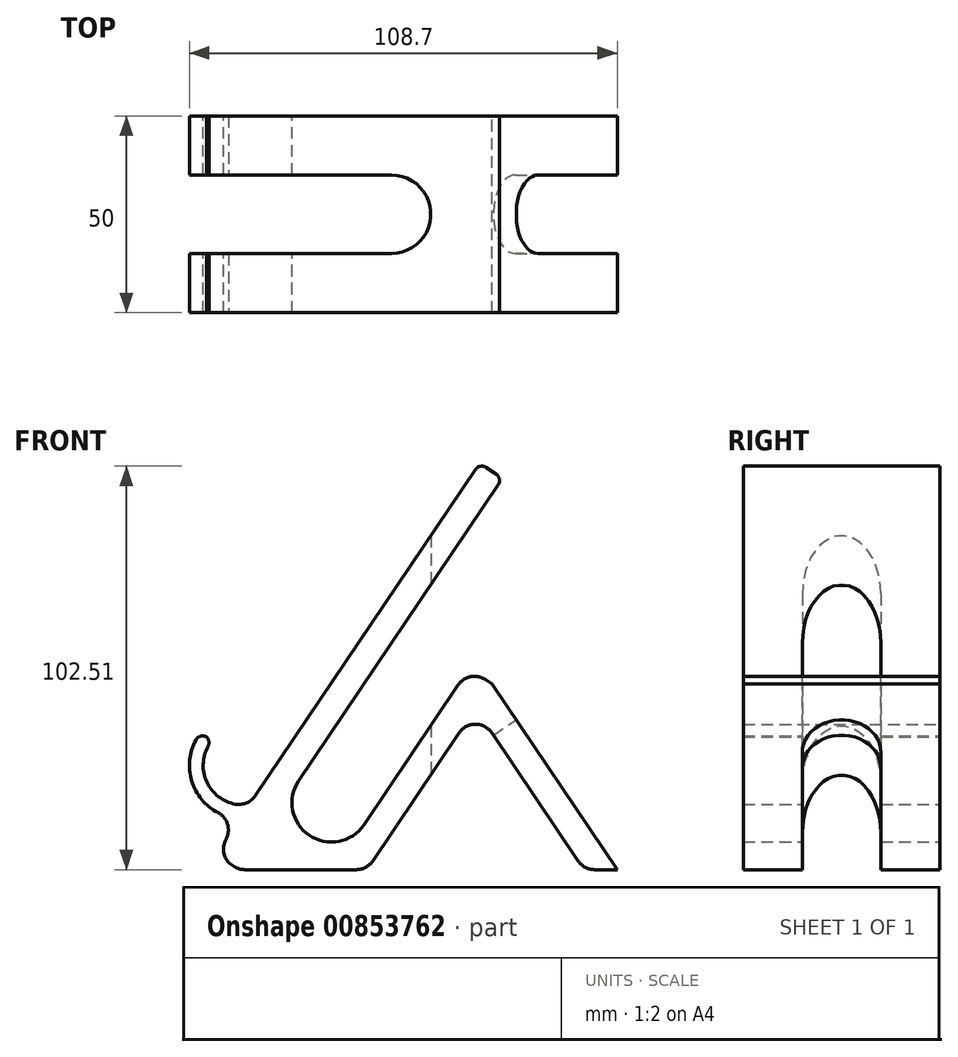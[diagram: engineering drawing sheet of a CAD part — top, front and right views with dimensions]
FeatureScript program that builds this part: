
annotation { "Feature Type Name" : "Feature", "Feature Type Description" : "" }
export const myFeature = defineFeature(function(context is Context, id is Id, definition is map)
    precondition{}
    {
        {
            var Q0;
            Q0=qCreatedBy(makeId("Front.planeOp"),FACE);
            var sketch = newSketch(context, id + "F0", { "sketchPlane" : qUnion([Q0])});
            skLineSegment(sketch, "E0", {"start": v(15.24, 22.6) * mm, "end": v(67.03, 99.37) * mm});
            skLineSegment(sketch, "E1", {"start": v(67.03, 99.37) * mm, "end": v(61.22, 103.29) * mm});
            skLineSegment(sketch, "E2", {"start": v(61.22, 103.29) * mm, "end": v(2.78, 16.63) * mm});
            skLineSegment(sketch, "E3", {"start": v(-5.88, 3.8) * mm, "end": v(0, 0) * mm});
            skArc(sketch, "E4", {"start": v(15.24, 22.6) * mm, "mid": v(17.94, 8.7) * mm, "end": v(31.82, 11.4) * mm});
            skLineSegment(sketch, "E5", {"start": v(-35.19, 0) * mm, "end": v(113.44, 0) * mm, "construction": true});
            skLineSegment(sketch, "E6", {"start": v(31.82, 11.4) * mm, "end": v(58.57, 51.06) * mm});
            skLineSegment(sketch, "E7", {"start": v(58.57, 51.06) * mm, "end": v(64.37, 47.15) * mm});
            skLineSegment(sketch, "E8", {"start": v(60.15, 40.89) * mm, "end": v(32.57, 0) * mm});
            skLineSegment(sketch, "E9", {"start": v(32.57, 0) * mm, "end": v(0, 0) * mm});
            skLineSegment(sketch, "E10", {"start": v(64.37, 47.15) * mm, "end": v(96.17, 0) * mm});
            skLineSegment(sketch, "E11", {"start": v(60.15, 40.89) * mm, "end": v(87.73, 0) * mm});
            skLineSegment(sketch, "E12", {"start": v(87.73, 0) * mm, "end": v(96.17, 0) * mm});
            skLineSegment(sketch, "E13", {"start": v(53.8, 104.81) * mm, "end": v(-7.27, 14.27) * mm, "construction": true});
            skArc(sketch, "E14", {"start": v(-6.78, 32.79) * mm, "mid": v(-7.64, 21.38) * mm, "end": v(2.78, 16.63) * mm});
            skArc(sketch, "E15", {"start": v(-9.67, 34.78) * mm, "mid": v(-11.3, 20.85) * mm, "end": v(0.31, 12.98) * mm});
            skLineSegment(sketch, "E16", {"start": v(-9.67, 34.78) * mm, "end": v(-6.78, 32.79) * mm});
            skLineSegment(sketch, "E17.trimOffspring", {"start": v(0.31, 12.98) * mm, "end": v(-5.88, 3.8) * mm});
            skSolve(sketch);
        }
        {
            var Q0;
            Q0=makeQuery(id+"F0.imprint","IMPRINT",FACE,{"disambiguationData":[TD([[makeQuery(id+"F0.imprint","IMPRINT",EDGE,{"derivedFrom":sQuery(id+"F0.wireOp",EDGE,"E0")}),1.0]])]});
            extrude(context, id + "F1", {"entities" : qUnion([Q0]), "depth" : 50 * mm, "offsetDistance" : 25 * mm});
        }
        {
            var Q0;
            Q0=makeQuery(id+"F1.opExtrude","SWEPT_EDGE",EDGE,{"disambiguationData":[OSD([sQuery(id+"F0.wireOp",EDGE,"E6"),sQuery(id+"F0.wireOp",EDGE,"E7")])]});
            var Q1;
            Q1=makeQuery(id+"F1.opExtrude","SWEPT_EDGE",EDGE,{"disambiguationData":[OSD([sQuery(id+"F0.wireOp",EDGE,"E8"),sQuery(id+"F0.wireOp",EDGE,"E11")])]});
            var Q2;
            Q2=makeQuery(id+"F1.opExtrude","SWEPT_EDGE",EDGE,{"disambiguationData":[OSD([sQuery(id+"F0.wireOp",EDGE,"E8"),sQuery(id+"F0.wireOp",EDGE,"E9")])]});
            var Q3;
            Q3=makeQuery(id+"F1.opExtrude","SWEPT_EDGE",EDGE,{"disambiguationData":[OSD([sQuery(id+"F0.wireOp",EDGE,"E11"),sQuery(id+"F0.wireOp",EDGE,"E12")])]});
            var Q4;
            Q4=makeQuery(id+"F1.opExtrude","SWEPT_EDGE",EDGE,{"disambiguationData":[OSD([sQuery(id+"F0.wireOp",EDGE,"E3"),sQuery(id+"F0.wireOp",EDGE,"E9")])]});
            var Q5;
            Q5=makeQuery(id+"F1.opExtrude","SWEPT_EDGE",EDGE,{"disambiguationData":[OSD([sQuery(id+"F0.wireOp",EDGE,"E3"),sQuery(id+"F0.wireOp",EDGE,"E17.trimOffspring")])]});
            fillet(context, id + "F2", {"entities" : qUnion([Q0, Q1, Q2, Q3, Q4, Q5]), "radius" : 5 * mm, "tangentPropagation" : true, "allowEdgeOverflow" : false});
        }
        {
            var Q0;
            Q0=makeQuery(id+"F1.opExtrude","SWEPT_EDGE",EDGE,{"disambiguationData":[OSD([sQuery(id+"F0.wireOp",EDGE,"E15"),sQuery(id+"F0.wireOp",EDGE,"E16")])]});
            var Q1;
            Q1=makeQuery(id+"F1.opExtrude","SWEPT_EDGE",EDGE,{"disambiguationData":[OSD([sQuery(id+"F0.wireOp",EDGE,"E14"),sQuery(id+"F0.wireOp",EDGE,"E16")])]});
            var Q2;
            Q2=makeQuery(id+"F1.opExtrude","SWEPT_EDGE",EDGE,{"disambiguationData":[OSD([sQuery(id+"F0.wireOp",EDGE,"E1"),sQuery(id+"F0.wireOp",EDGE,"E2")])]});
            var Q3;
            Q3=makeQuery(id+"F1.opExtrude","SWEPT_EDGE",EDGE,{"disambiguationData":[OSD([sQuery(id+"F0.wireOp",EDGE,"E0"),sQuery(id+"F0.wireOp",EDGE,"E1")])]});
            fillet(context, id + "F3", {"entities" : qUnion([Q0, Q1, Q2, Q3]), "radius" : 2 * mm, "tangentPropagation" : true, "allowEdgeOverflow" : false});
        }
        {
            var Q0;
            Q0=makeQuery(id+"F1.opExtrude","SWEPT_EDGE",EDGE,{"disambiguationData":[OSD([sQuery(id+"F0.wireOp",EDGE,"E2"),sQuery(id+"F0.wireOp",EDGE,"E14")])]});
            var Q1;
            Q1=makeQuery(id+"F1.opExtrude","SWEPT_EDGE",EDGE,{"disambiguationData":[OSD([sQuery(id+"F0.wireOp",EDGE,"E15"),sQuery(id+"F0.wireOp",EDGE,"E17.trimOffspring")])]});
            fillet(context, id + "F4", {"entities" : qUnion([Q0, Q1]), "radius" : 5 * mm, "tangentPropagation" : true, "allowEdgeOverflow" : false});
        }
        {
            var Q0;
            Q0=makeQuery(id+"F1.opExtrude","SWEPT_FACE",FACE,{"disambiguationData":[OSD([sQuery(id+"F0.wireOp",EDGE,"E9")])]});
            var sketch = newSketch(context, id + "F5", { "sketchPlane" : qUnion([Q0])});
            skLineSegment(sketch, "E18", {"start": v(-32.55, 25) * mm, "end": v(103.24, 25) * mm, "construction": true});
            skArc(sketch, "E19", {"start": v(38.81, 15) * mm, "mid": v(48.81, 25) * mm, "end": v(38.81, 35) * mm});
            skLineSegment(sketch, "E20", {"start": v(38.81, 35) * mm, "end": v(-33.86, 35) * mm});
            skLineSegment(sketch, "E21", {"start": v(38.81, 15) * mm, "end": v(-33.86, 15) * mm});
            skLineSegment(sketch, "E22", {"start": v(-33.86, 15) * mm, "end": v(-33.86, 35) * mm});
            skSolve(sketch);
        }
        {
            var Q0;
            {var subQ0=sQuery(id+"F5.wireOp",EDGE,"E22");Q0=makeQuery(id+"F5.imprint","IMPRINT",FACE,{"disambiguationData":[TD([[makeQuery(id+"F5.imprint","IMPRINT",EDGE,{"derivedFrom":subQ0}),-1.0]])]});}
            var Q1;
            {var subQ0=sQuery(id+"F5.wireOp",EDGE,"E20");var subQ1=sQuery(id+"F0.wireOp",EDGE,"E9");var subQ2=makeQuery(id+"F1.opExtrude","SWEPT_FACE",FACE,{"disambiguationData":[OSD([subQ1])]});var subQ3=makeQuery(id+"F2.opFillet","BLEND_EDGE",EDGE,{"blendedFrom":[makeQuery(id+"F1.opExtrude","SWEPT_EDGE",EDGE,{"disambiguationData":[OSD([sQuery(id+"F0.wireOp",EDGE,"E8"),subQ1])]}),subQ2],"blendedInto":[subQ2]});var subQ4=makeQuery(id+"F5.imprint","INTERSECT",VERTEX,{"derivedFrom":[subQ3,subQ0]});Q1=makeQuery(id+"F5.imprint","IMPRINT",FACE,{"disambiguationData":[TD([[makeQuery(id+"F5.imprint","IMPRINT",EDGE,{"disambiguationData":[TD([[subQ4,-1.0]])],"derivedFrom":subQ0}),1.0]])]});}
            var Q2;
            {var subQ0=sQuery(id+"F5.wireOp",EDGE,"E19");Q2=makeQuery(id+"F5.imprint","IMPRINT",FACE,{"disambiguationData":[TD([[makeQuery(id+"F5.imprint","IMPRINT",EDGE,{"derivedFrom":subQ0}),1.0]])]});}
            extrude(context, id + "F6", {"entities" : qUnion([Q0, Q1, Q2]), "operationType" : NewBodyOperationType.REMOVE, "oppositeDirection" : true, "depth" : 102.5 * mm, "offsetDistance" : 25 * mm});
        }
        {
            var Q0;
            Q0=makeQuery(id+"F1.opExtrude","SWEPT_FACE",FACE,{"disambiguationData":[OSD([sQuery(id+"F0.wireOp",EDGE,"E10")])]});
            var sketch = newSketch(context, id + "F7", { "sketchPlane" : qUnion([Q0])});
            skLineSegment(sketch, "E23", {"start": v(-25, -74.02) * mm, "end": v(-25, 61.94) * mm, "construction": true});
            skArc(sketch, "E24", {"start": v(-15, -17.86) * mm, "mid": v(-25, -7.86) * mm, "end": v(-35, -17.86) * mm});
            skLineSegment(sketch, "E25", {"start": v(-15, -17.86) * mm, "end": v(-15, -68.69) * mm});
            skLineSegment(sketch, "E26", {"start": v(-15, -68.69) * mm, "end": v(-35, -68.69) * mm});
            skLineSegment(sketch, "E27", {"start": v(-35, -68.69) * mm, "end": v(-35, -17.86) * mm});
            skSolve(sketch);
        }
        {
            var Q0;
            {var subQ0=sQuery(id+"F7.wireOp",EDGE,"E24");Q0=makeQuery(id+"F7.imprint","IMPRINT",FACE,{"disambiguationData":[TD([[makeQuery(id+"F7.imprint","IMPRINT",EDGE,{"derivedFrom":subQ0}),1.0]])]});}
            extrude(context, id + "F8", {"entities" : qUnion([Q0]), "operationType" : NewBodyOperationType.REMOVE, "oppositeDirection" : true, "depth" : 25 * mm, "offsetDistance" : 25 * mm});
        }
    });
